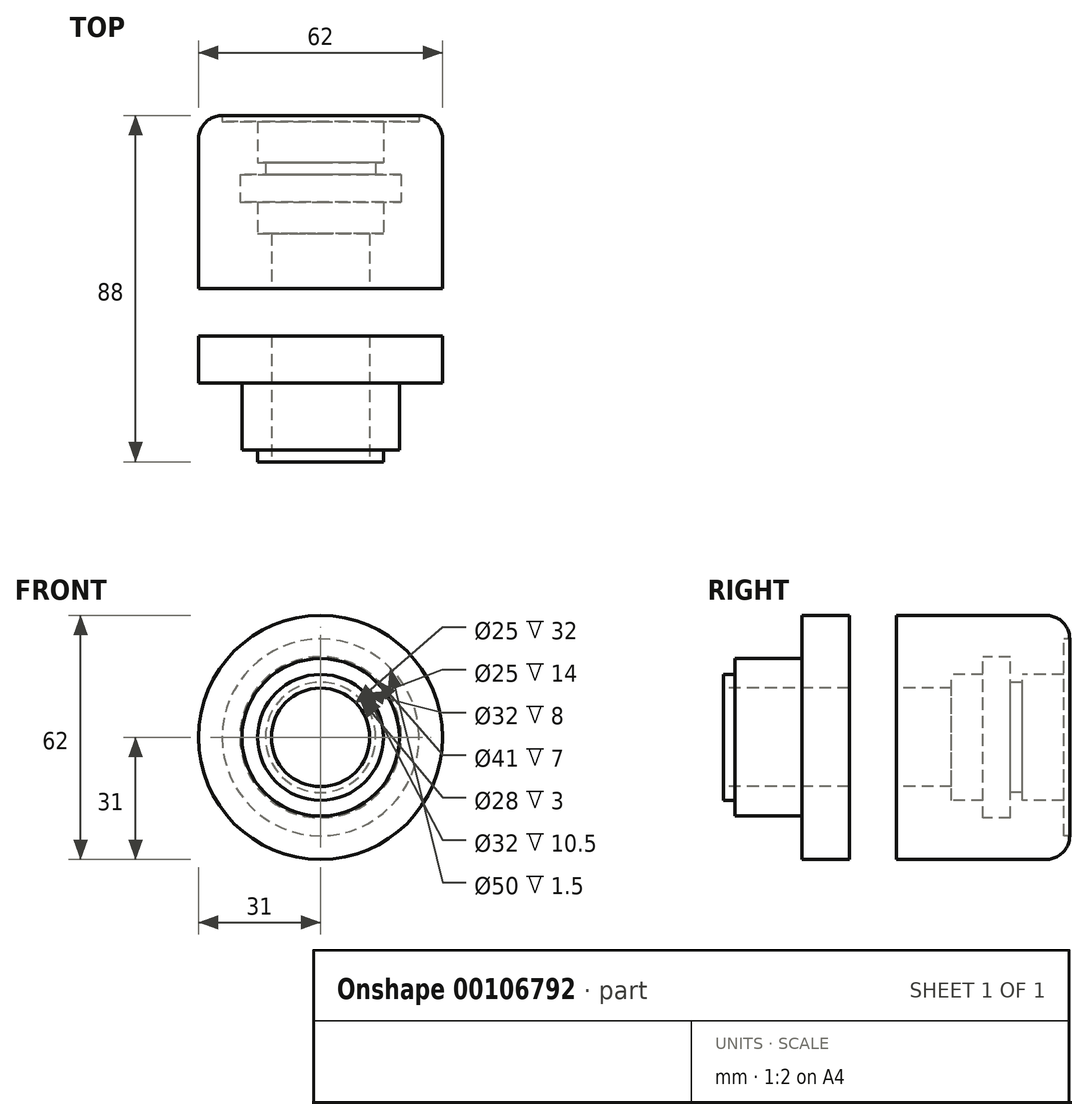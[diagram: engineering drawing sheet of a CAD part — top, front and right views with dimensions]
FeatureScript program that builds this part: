
annotation { "Feature Type Name" : "Feature", "Feature Type Description" : "" }
export const myFeature = defineFeature(function(context is Context, id is Id, definition is map)
    precondition{}
    {
        {
            var Q0;
            Q0=qCreatedBy(makeId("Right.planeOp"),FACE);
            var sketch = newSketch(context, id + "F0", { "sketchPlane" : qUnion([Q0])});
            skLineSegment(sketch, "E0", {"start": v(-42.75, 0) * mm, "end": v(60.44, 0) * mm, "construction": true});
            skArc(sketch, "E1", {"start": v(6, 31) * mm, "mid": v(0, 25) * mm, "end": v(-6, 31) * mm});
            skLineSegment(sketch, "E2.bottom", {"start": v(-38, 12.5) * mm, "end": v(-35, 12.5) * mm});
            skLineSegment(sketch, "E2.top", {"start": v(-38, 16) * mm, "end": v(-35, 16) * mm});
            skLineSegment(sketch, "E2.left", {"start": v(-38, 12.5) * mm, "end": v(-38, 16) * mm});
            skLineSegment(sketch, "E2.right", {"start": v(-35, 12.5) * mm, "end": v(-35, 16) * mm});
            skLineSegment(sketch, "E3.bottom", {"start": v(-35, 12.5) * mm, "end": v(-18, 12.5) * mm});
            skLineSegment(sketch, "E3.top", {"start": v(-35, 20) * mm, "end": v(-18, 20) * mm});
            skLineSegment(sketch, "E3.left", {"start": v(-35, 12.5) * mm, "end": v(-35, 20) * mm});
            skLineSegment(sketch, "E3.right", {"start": v(-18, 12.5) * mm, "end": v(-18, 20) * mm});
            skLineSegment(sketch, "E4.bottom", {"start": v(-18, 12.5) * mm, "end": v(-6, 12.5) * mm});
            skLineSegment(sketch, "E4.top", {"start": v(-18, 31) * mm, "end": v(-6, 31) * mm});
            skLineSegment(sketch, "E4.left", {"start": v(-18, 12.5) * mm, "end": v(-18, 31) * mm});
            skLineSegment(sketch, "E4.right", {"start": v(-6, 12.5) * mm, "end": v(-6, 31) * mm});
            skLineSegment(sketch, "E5.bottom", {"start": v(6, 31) * mm, "end": v(50, 31) * mm});
            skLineSegment(sketch, "E5.top", {"start": v(6, 12.5) * mm, "end": v(50, 12.5) * mm});
            skLineSegment(sketch, "E5.left", {"start": v(6, 31) * mm, "end": v(6, 12.5) * mm});
            skLineSegment(sketch, "E5.right", {"start": v(50, 31) * mm, "end": v(50, 12.5) * mm});
            skLineSegment(sketch, "E6", {"start": v(-38, 12.5) * mm, "end": v(20, 12.5) * mm});
            skLineSegment(sketch, "E7.bottom", {"start": v(20, 12.5) * mm, "end": v(28, 12.5) * mm});
            skLineSegment(sketch, "E7.top", {"start": v(20, 16) * mm, "end": v(28, 16) * mm});
            skLineSegment(sketch, "E7.left", {"start": v(20, 12.5) * mm, "end": v(20, 16) * mm});
            skLineSegment(sketch, "E7.right", {"start": v(28, 12.5) * mm, "end": v(28, 16) * mm});
            skLineSegment(sketch, "E8.bottom", {"start": v(28, 20.5) * mm, "end": v(35, 20.5) * mm});
            skLineSegment(sketch, "E8.top", {"start": v(28, 12.5) * mm, "end": v(35, 12.5) * mm});
            skLineSegment(sketch, "E8.left", {"start": v(28, 20.5) * mm, "end": v(28, 12.5) * mm});
            skLineSegment(sketch, "E8.right", {"start": v(35, 20.5) * mm, "end": v(35, 12.5) * mm});
            skLineSegment(sketch, "E9.bottom", {"start": v(35, 12.5) * mm, "end": v(38, 12.5) * mm});
            skLineSegment(sketch, "E9.top", {"start": v(35, 14) * mm, "end": v(38, 14) * mm});
            skLineSegment(sketch, "E9.left", {"start": v(35, 12.5) * mm, "end": v(35, 14) * mm});
            skLineSegment(sketch, "E9.right", {"start": v(38, 12.5) * mm, "end": v(38, 14) * mm});
            skLineSegment(sketch, "E10.bottom", {"start": v(38, 12.5) * mm, "end": v(48.5, 12.5) * mm});
            skLineSegment(sketch, "E10.top", {"start": v(38, 16) * mm, "end": v(48.5, 16) * mm});
            skLineSegment(sketch, "E10.left", {"start": v(38, 12.5) * mm, "end": v(38, 16) * mm});
            skLineSegment(sketch, "E10.right", {"start": v(48.5, 12.5) * mm, "end": v(48.5, 16) * mm});
            skLineSegment(sketch, "E11.bottom", {"start": v(48.5, 12.5) * mm, "end": v(50, 12.5) * mm});
            skLineSegment(sketch, "E11.top", {"start": v(48.5, 25) * mm, "end": v(50, 25) * mm});
            skLineSegment(sketch, "E11.left", {"start": v(48.5, 12.5) * mm, "end": v(48.5, 25) * mm});
            skLineSegment(sketch, "E11.right", {"start": v(50, 12.5) * mm, "end": v(50, 25) * mm});
            skSolve(sketch);
        }
        {
            var Q0;
            {var subQ0=sQuery(id+"F0.wireOp",EDGE,"E2.top");Q0=makeQuery(id+"F0.imprint","IMPRINT",FACE,{"disambiguationData":[TD([[makeQuery(id+"F0.imprint","IMPRINT",EDGE,{"derivedFrom":subQ0}),-1.0]])]});}
            var Q1;
            {var subQ1=sQuery(id+"F0.wireOp",EDGE,"E3.top");Q1=makeQuery(id+"F0.imprint","IMPRINT",FACE,{"disambiguationData":[TD([[makeQuery(id+"F0.imprint","IMPRINT",EDGE,{"derivedFrom":subQ1}),-1.0]])]});}
            var Q2;
            {var subQ3=sQuery(id+"F0.wireOp",EDGE,"E4.top");Q2=makeQuery(id+"F0.imprint","IMPRINT",FACE,{"disambiguationData":[TD([[makeQuery(id+"F0.imprint","IMPRINT",EDGE,{"derivedFrom":subQ3}),-1.0]])]});}
            var Q3;
            Q3=makeQuery(id+"F0.imprint","IMPRINT",FACE,{"disambiguationData":[TD([[makeQuery(id+"F0.imprint","IMPRINT",EDGE,{"derivedFrom":sQuery(id+"F0.wireOp",EDGE,"E1")}),1.0]])]});
            var Q4;
            Q4=makeQuery(id+"F0.imprint","IMPRINT",FACE,{"disambiguationData":[TD([[makeQuery(id+"F0.imprint","IMPRINT",EDGE,{"derivedFrom":sQuery(id+"F0.wireOp",EDGE,"E5.bottom")}),-1.0]])]});
            var Q5;
            Q5=sQuery(id+"F0.wireOp",EDGE,"E0");
            revolve(context, id + "F1", {"entities" : qUnion([Q0, Q1, Q2, Q3, Q4]), "axis" : qUnion([Q5]), "revolveType" : RevolveType.FULL});
        }
        {
            var Q0;
            Q0=makeQuery(id+"F1.opRevolve","SWEPT_EDGE",EDGE,{"disambiguationData":[OSD([sQuery(id+"F0.wireOp",EDGE,"E5.bottom"),sQuery(id+"F0.wireOp",EDGE,"E5.right")])]});
            fillet(context, id + "F2", {"entities" : qUnion([Q0]), "radius" : 6 * mm, "tangentPropagation" : true, "allowEdgeOverflow" : false});
        }
    });
